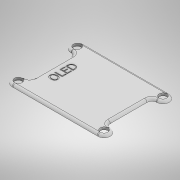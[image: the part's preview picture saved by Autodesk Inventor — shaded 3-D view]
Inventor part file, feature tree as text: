
AUTODESK INVENTOR PART (.ipt)
format: ipt  version: 2021 (Build 250183000, 183)  size: 295,424 bytes
history: native  units: mm
features: sketch x3, extrude x2, fillet x2, emboss x1
ambient origin geometry x8: Origin, YZ Plane, XZ Plane, XY Plane, X Axis, Y Axis, Z Axis, Center Point
bodies: Solid1 (feature_tree)
feature tree (8):
  extrude  "Extrusion1"  Depth=25.0mm
  fillet  "Fillet2"  Radius=2.0mm
  fillet  "Fillet3"  Radius=2.0mm
  emboss  "Emboss2"
  extrude  "Extrusion3"  Depth=1.0mm TaperAngle=0.0deg
  sketch  "Sketch1"  dims[d0=27.0mm d1=25.0mm d12=2.0mm d14=2.0mm]
  sketch  "Sketch4"  dims[d15=2.0mm d16=1.0mm d17=0.0mm]
  sketch  "Sketch5"  dims[d22=5.0mm d23=2.5mm d24=2.0mm d25=2.5mm d26=2.0mm d27=5.0mm d28=5.0mm d29=5.0mm d30=2.0mm d31=2.0mm d32=2.5mm d33=2.5mm d34=3.1mm d35=3.1mm d36=3.1mm d37=3.1mm d47=2.0mm d48=2.0mm d49=7.5mm d50=14.0mm d51=2.0mm d52=1.0mm d56=0.2mm d57=0.0mm d58=0.5mm d59=10.0mm d60=0.0mm]
